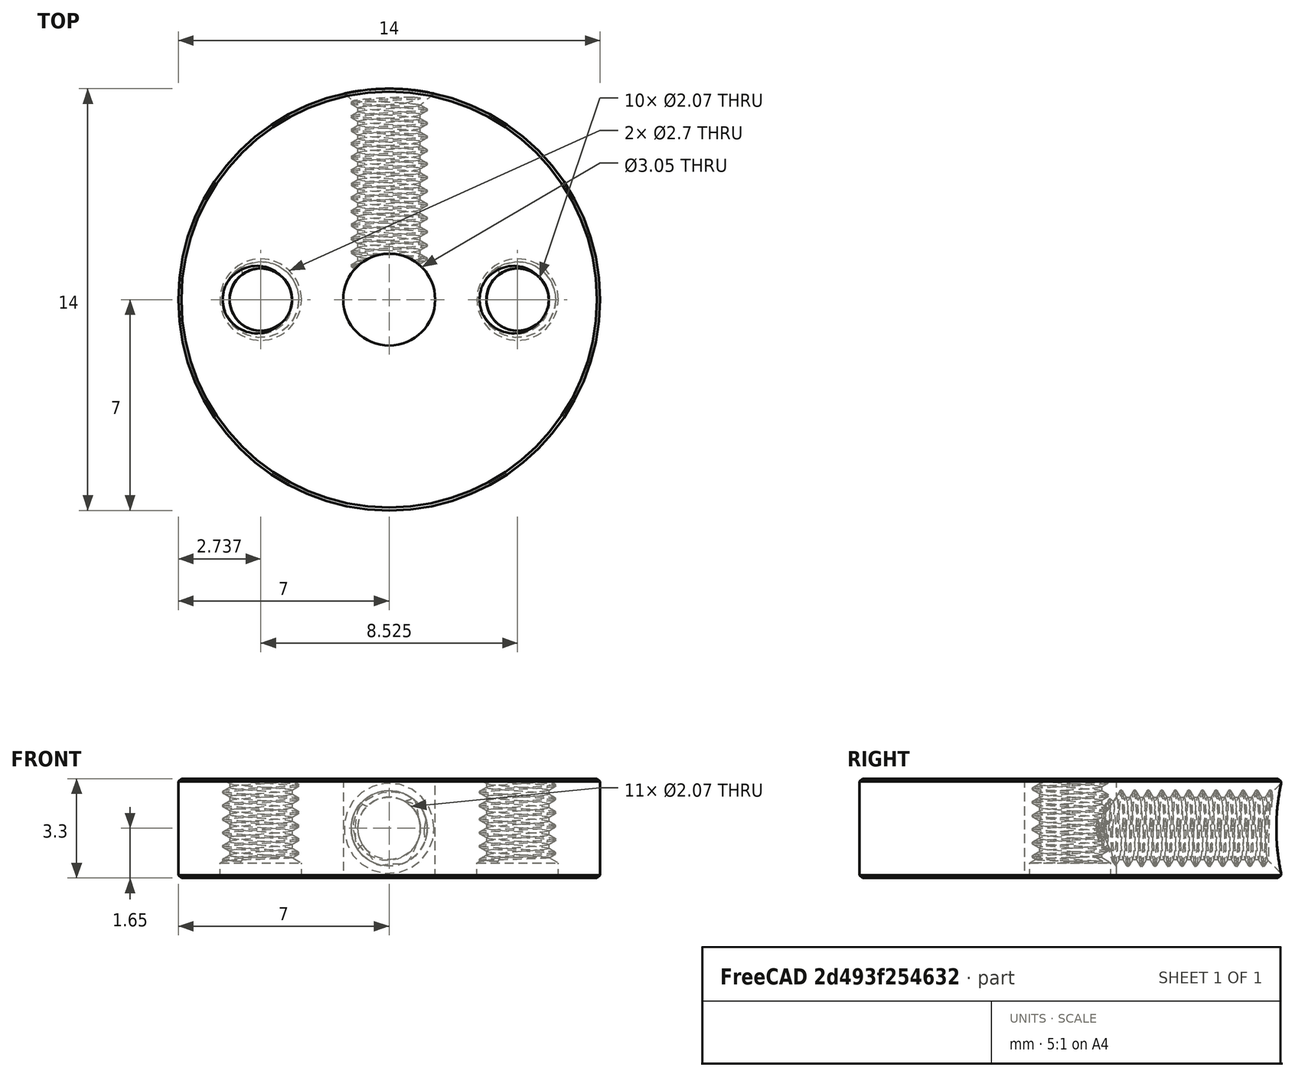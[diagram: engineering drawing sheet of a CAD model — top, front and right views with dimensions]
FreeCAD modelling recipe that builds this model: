
FCSTD DOCUMENT  (FreeCAD 0.20R29603 (Git))
Label: shaft-collar-relieved
License: Other
objects: TechDraw::DrawViewAnnotation×5, TechDraw::DrawViewDimension×4, Sketcher::SketchObject×3, PartDesign::Hole×3, TechDraw::DrawProjGroupItem×3, TechDraw::DrawViewSection×3, TechDraw::DrawViewBalloon×3, PartDesign::Chamfer×2, PartDesign::Pad×1, TechDraw::DrawSVGTemplate×1, PartDesign::Plane×1, PartDesign::Pocket×1, PartDesign::Body×1, TechDraw::DrawProjGroup×1, TechDraw::DrawRichAnno×1, TechDraw::DrawLeaderLine×1, TechDraw::DrawPage×1
note: 19 computed .brp shape members not serialized (recipe doc carries the construction recipe); baked Part::Feature solids carry a one-line shape summary decoded from their .brp

FEATURE [Sketcher::SketchObject] Sketch
  FullyConstrained = true
  MapMode = 5
  Support = -> [XY_Plane]
  sketch-geometry (5):
    g0: Circle CenterX=0 CenterY=0 CenterZ=0 NormalX=0 NormalY=0 NormalZ=1 AngleXU=0 Radius=7
    g1: Circle CenterX=0 CenterY=0 CenterZ=0 NormalX=0 NormalY=0 NormalZ=1 AngleXU=0 Radius=1.525
    g2: LineSegment StartX=1.525 StartY=0 StartZ=0 EndX=7 EndY=0 EndZ=0
    g3: Circle CenterX=4.2625 CenterY=0 CenterZ=0 NormalX=0 NormalY=0 NormalZ=1 AngleXU=0 Radius=1
    g4: Circle CenterX=-4.2625 CenterY=0 CenterZ=0 NormalX=0 NormalY=0 NormalZ=1 AngleXU=0 Radius=1
  constraints (15):
    c: Coincident(g1,g0)
    c: Coincident(g0,g-1)
    c: Diameter(g1) = 3.05
    c: Diameter(g0) = 14
    c: PointOnObject(g2,g1)
    c: PointOnObject(g2,g0)
    c: Horizontal(g2)
    c: PointOnObject(g2,g-1)
    c: DistanceX(g2,g2) = 5.475
    c: Symmetric(g2,g2,g3)
    c: Diameter(g3) = 2
    c: DistanceX(g2,g3) = 2.7375
    c: Symmetric(g3,g4,g-2)
    c: Equal(g4,g3)
    c: DistanceX(g4,g3) = 8.525
FEATURE [PartDesign::Pad] Pad
  Direction = (0,0,1)
  Length = 3.3
  Length2 = 10
  Profile = -> Sketch
  ReferenceAxis = -> Sketch [N_Axis]
  Type = 0
FEATURE [Sketcher::SketchObject] Sketch001
  ExternalGeometry = -> [Pad,Sketch]
  FullyConstrained = true
  MapMode = 5
  Placement = pos=(0,0,0) rot=(1,0,0;1.5708rad)
  Support = -> [XZ_Plane]
  sketch-geometry (3):
    g0: GeomPoint X=0 Y=1.65 Z=0
    g1: Circle CenterX=0 CenterY=1.65 CenterZ=0 NormalX=0 NormalY=0 NormalZ=1 AngleXU=0 Radius=1
    g2: LineSegment StartX=0 StartY=0 StartZ=0 EndX=0 EndY=3.3 EndZ=0
  constraints (7):
    c: PointOnObject(g0,g-2)
    c: Coincident(g1,g0)
    c: DistanceY(g-1,g1) = 1.65
    c: Coincident(g2,g-1)
    c: PointOnObject(g2,g-3)
    c: Symmetric(g2,g2,g1)
    c: Diameter(g1) = 2
FEATURE [TechDraw::DrawSVGTemplate] Template
  EditableTexts = Designed_by_Name=Lucian Chapar; Drawing_number=N/A; FC-Date=2023-02-15; FC-SC=4:1; FC-SH=1 OF 1; FC-Title=drive-wheel-shaft-collar-alt; Weight=N/A
  Height = 210
  Orientation = 1
  Width = 297
FEATURE [PartDesign::Hole] Hole
  BaseFeature = -> Pad
  CustomThreadClearance = 0
  Depth = 0.5
  DepthType = 0
  Diameter = 2.7
  DrillForDepth = false
  DrillPoint = 1
  DrillPointAngle = 118
  HoleCutCountersinkAngle = 90
  HoleCutCustomValues = false
  HoleCutDepth = 0
  HoleCutDiameter = 6.1
  HoleCutType = 0
  ModelThread = false
  Profile = -> Pad [Edge8,Edge11]
  Reversed = true
  Tapered = false
  TaperedAngle = 90
  ThreadClass = 0
  ThreadDepth = 0.5
  ThreadDepthType = 0
  ThreadDirection = 0
  ThreadFit = 0
  ThreadSize = 0
  ThreadType = 0
  Threaded = false
  UseCustomThreadClearance = false
FEATURE [PartDesign::Hole] Hole001
  BaseFeature = -> Hole
  CustomThreadClearance = 0
  Depth = 25
  DepthType = 0
  Diameter = 2.07
  DrillForDepth = false
  DrillPoint = 1
  DrillPointAngle = 118
  HoleCutCountersinkAngle = 90
  HoleCutCustomValues = false
  HoleCutDepth = 0
  HoleCutDiameter = 6.1
  HoleCutType = 0
  ModelThread = true
  Profile = -> Hole [Edge9,Edge8]
  Tapered = false
  TaperedAngle = 90
  ThreadClass = 0
  ThreadDepth = 25
  ThreadDepthType = 0
  ThreadDirection = 0
  ThreadFit = 0
  ThreadSize = 8
  ThreadType = 1
  Threaded = true
  UseCustomThreadClearance = false
FEATURE [PartDesign::Plane] DatumPlane
  AttachmentOffset = pos=(0,0,-7) rot=(0,0,1;0rad)
  Length = 60
  MapMode = 5
  Placement = pos=(0,7,1.6e-15) rot=(1,0,0;1.5708rad)
  ResizeMode = 0
  Support = -> [XZ_Plane]
  Width = 60
FEATURE [Sketcher::SketchObject] Sketch002
  ExternalGeometry = -> [Sketch001]
  FullyConstrained = true
  MapMode = 5
  Placement = pos=(0,7,1.6e-15) rot=(1,0,0;1.5708rad)
  Support = -> [DatumPlane]
  sketch-geometry (1):
    g0: Circle CenterX=0 CenterY=1.65 CenterZ=0 NormalX=0 NormalY=0 NormalZ=1 AngleXU=0 Radius=1
  constraints (3):
    c: Coincident(g0,g-3)
    c: Diameter(g-3) = 2
    c: Diameter(g0) = 2
FEATURE [PartDesign::Pocket] Pocket
  BaseFeature = -> Hole001
  Direction = (0,1,2e-16)
  Length = 7
  Length2 = 5
  Profile = -> Sketch002
  ReferenceAxis = -> Sketch002 [N_Axis]
  Reversed = true
  Type = 0
FEATURE [PartDesign::Chamfer] Chamfer
  Angle = 45
  Base = -> Pocket [Edge5,Edge4,Edge6]
  BaseFeature = -> Pocket
  ChamferType = 0
  FlipDirection = false
  Size = 0.5
  Size2 = 1
  SupportTransform = false
  UseAllEdges = false
FEATURE [PartDesign::Hole] Hole002
  BaseFeature = -> Chamfer
  CustomThreadClearance = 0
  Depth = 25
  DepthType = 0
  Diameter = 2.07
  DrillForDepth = false
  DrillPoint = 1
  DrillPointAngle = 118
  HoleCutCountersinkAngle = 90
  HoleCutCustomValues = false
  HoleCutDepth = 0
  HoleCutDiameter = 6.1
  HoleCutType = 0
  ModelThread = true
  Profile = -> Sketch001
  Tapered = false
  TaperedAngle = 90
  ThreadClass = 0
  ThreadDepth = 25
  ThreadDepthType = 0
  ThreadDirection = 0
  ThreadFit = 0
  ThreadSize = 8
  ThreadType = 1
  Threaded = true
  UseCustomThreadClearance = false
FEATURE [TechDraw::DrawViewAnnotation] Annotation
  Font = osifont
  LineSpace = 80
  LockPosition = false
  MaxWidth = -1
  Rotation = 0
  ScaleType = 0
  Text = Section A-A
  TextSize = 5
  TextStyle = 0
  X = 213.839
  Y = 106.01
FEATURE [TechDraw::DrawViewAnnotation] Annotation001
  Font = osifont
  LineSpace = 80
  LockPosition = false
  MaxWidth = -1
  Rotation = 0
  ScaleType = 0
  Text = Section B-B
  TextSize = 5
  TextStyle = 0
  X = 213.919
  Y = 187.915
FEATURE [TechDraw::DrawViewAnnotation] Annotation002
  Font = osifont
  LineSpace = 80
  LockPosition = false
  MaxWidth = -1
  Rotation = 0
  ScaleType = 0
  Text = Section C - C
  TextSize = 5
  TextStyle = 0
  X = 265.047
  Y = 115.508
FEATURE [TechDraw::DrawViewAnnotation] Annotation003
  Font = osifont
  LineSpace = 80
  LockPosition = false
  MaxWidth = -1
  Rotation = 0
  ScaleType = 0
  Text = OPULO INC
  TextSize = 5
  TextStyle = 0
  X = 203.475
  Y = 31.1769
FEATURE [PartDesign::Chamfer] Chamfer001
  Angle = 45
  Base = -> Hole002 [Edge2,Edge4]
  BaseFeature = -> Hole002
  ChamferType = 0
  FlipDirection = false
  Size = 0.1
  Size2 = 1
  SupportTransform = false
  UseAllEdges = false
FEATURE [PartDesign::Body] Body
  Group = -> [Sketch,Pad,Sketch001,Hole,Hole001,DatumPlane,Sketch002,Pocket,Chamfer,Hole002,Chamfer001]
  Origin = -> Origin
  Tip = -> Chamfer001
FEATURE [TechDraw::DrawProjGroupItem] ProjItem  label="Top002"
  CoarseView = false
  Direction = (0,0,1)
  Focus = 100
  HardHidden = false
  IsoCount = 0
  IsoHidden = false
  IsoVisible = false
  LockPosition = true
  Perspective = false
  Rotation = 0
  RotationVector = (1,0,0)
  Scale = 4
  ScaleType = 2
  SeamHidden = false
  SeamVisible = true
  SmoothHidden = false
  SmoothVisible = true
  Source = -> [Body]
  Type = 5
  X = 0
  XDirection = (1,0,0)
  Y = 0
FEATURE [TechDraw::DrawProjGroupItem] ProjItem001  label="Front"
  CoarseView = false
  Direction = (0,1,0)
  Focus = 100
  HardHidden = false
  IsoCount = 0
  IsoHidden = false
  IsoVisible = false
  LockPosition = false
  Perspective = false
  Rotation = 0
  RotationVector = (1,0,0)
  ScaleType = 2
  SeamHidden = false
  SeamVisible = true
  SmoothHidden = false
  SmoothVisible = true
  Source = -> [Body]
  Type = 4
  X = 0
  XDirection = (1,0,0)
  Y = -55.9883
FEATURE [TechDraw::DrawProjGroupItem] ProjItem002  label="Left"
  CoarseView = false
  Direction = (-1,0,1e-16)
  Focus = 100
  HardHidden = false
  IsoCount = 0
  IsoHidden = false
  IsoVisible = false
  LockPosition = false
  Perspective = false
  Rotation = 0
  RotationVector = (1,0,0)
  ScaleType = 2
  SeamHidden = false
  SeamVisible = true
  SmoothHidden = false
  SmoothVisible = true
  Source = -> [Body]
  Type = 1
  X = 55
  XDirection = (1e-16,0,1)
  Y = 0
FEATURE [TechDraw::DrawProjGroup] ProjGroup
  Anchor = -> ProjItem
  AutoDistribute = false
  LockPosition = false
  ProjectionType = 0
  Rotation = 0
  Scale = 4
  ScaleType = 2
  Source = -> [Body]
  Views = -> [ProjItem,ProjItem001,ProjItem002]
  X = 61.8769
  Y = 150
  spacingX = 15
  spacingY = 15
FEATURE [TechDraw::DrawViewSection] SectionView001  label="Section A - A"
  BaseView = -> ProjItem
  CoarseView = false
  CutSurfaceDisplay = 2
  Direction = (0,-1,0)
  FileGeomPattern = /Applications/FreeCAD.app/Contents/Resources/share/Mod/TechDraw/PAT/FCPAT.pat
  FileHatchPattern = /Applications/FreeCAD.app/Contents/Resources/share/Mod/TechDraw/Patterns/simple.svg
  Focus = 100
  FuseBeforeCut = false
  HardHidden = false
  HatchScale = 1
  IsoCount = 0
  IsoHidden = false
  IsoVisible = false
  LockPosition = false
  NameGeomPattern = Diamond
  Perspective = false
  Rotation = 0
  Scale = 4
  ScaleType = 2
  SeamHidden = false
  SeamVisible = true
  SectionDirection = 2
  SectionNormal = (0,-1,0)
  SectionOrigin = (0.013,0.003,1.65)
  SectionSymbol = A
  SmoothHidden = false
  SmoothVisible = true
  Source = -> [Body]
  X = 215.276
  XDirection = (1,0,0)
  Y = 93.815
FEATURE [TechDraw::DrawViewDimension] Dimension005
  AngleOverride = false
  Arbitrary = false
  ArbitraryTolerances = false
  EqualTolerance = false
  ExtensionAngle = 0
  FormatSpec = ⌀%.2w
  FormatSpecOverTolerance = %+.2w
  FormatSpecUnderTolerance = %+.2w
  Inverted = false
  LineAngle = 0
  LockPosition = false
  MeasureType = 1
  OverTolerance = 0
  References2D = -> [SectionView001]
  Rotation = 0
  ScaleType = 0
  TheoreticalExact = false
  Type = 1
  UnderTolerance = -0.2
  X = 35.0716
  Y = 16.5241
FEATURE [TechDraw::DrawViewBalloon] Balloon005
  BubbleShape = 1
  EndType = 0
  EndTypeScale = 1
  KinkLength = 5
  LockPosition = false
  OriginX = 0.164571
  OriginY = -1.02183
  Rotation = 0
  ScaleType = 0
  ShapeScale = 1
  SourceView = -> SectionView001
  Text = M2.5x0.45 ↧ 7
  TextWrapLen = -1
  X = 6.70793
  Y = -4.88619
FEATURE [TechDraw::DrawViewBalloon] Balloon006
  BubbleShape = 1
  EndType = 0
  EndTypeScale = 1
  KinkLength = 13
  LockPosition = false
  OriginX = -5.6125
  OriginY = -1.65
  Rotation = 0
  ScaleType = 0
  ShapeScale = 1
  SourceView = -> SectionView001
  TextWrapLen = -1
  X = -11.2435
  Y = -6.5218
FEATURE [TechDraw::DrawViewSection] SectionView  label="Section C - C"
  BaseView = -> ProjItem001
  CoarseView = false
  CutSurfaceDisplay = 2
  Direction = (-1,0,0)
  FileGeomPattern = /Applications/FreeCAD.app/Contents/Resources/share/Mod/TechDraw/PAT/FCPAT.pat
  FileHatchPattern = /Applications/FreeCAD.app/Contents/Resources/share/Mod/TechDraw/Patterns/simple.svg
  Focus = 100
  FuseBeforeCut = false
  HardHidden = false
  HatchScale = 1
  IsoCount = 0
  IsoHidden = false
  IsoVisible = false
  LockPosition = false
  NameGeomPattern = Diamond
  Perspective = false
  Rotation = 90
  Scale = 4
  ScaleType = 2
  SeamHidden = false
  SeamVisible = true
  SectionDirection = 0
  SectionNormal = (-1,0,0)
  SectionOrigin = (0.013,0.003,1.65)
  SectionSymbol = C
  SmoothHidden = false
  SmoothVisible = true
  Source = -> [Body]
  X = 265.52
  XDirection = (0,1,0)
  Y = 150
FEATURE [TechDraw::DrawViewSection] SectionView002  label="Section B - B"
  BaseView = -> ProjItem002
  CoarseView = false
  CutSurfaceDisplay = 2
  Direction = (1e-16,0,1)
  FileGeomPattern = /Applications/FreeCAD.app/Contents/Resources/share/Mod/TechDraw/PAT/FCPAT.pat
  FileHatchPattern = /Applications/FreeCAD.app/Contents/Resources/share/Mod/TechDraw/Patterns/simple.svg
  Focus = 100
  FuseBeforeCut = false
  HardHidden = false
  HatchScale = 1
  IsoCount = 0
  IsoHidden = false
  IsoVisible = false
  LockPosition = false
  NameGeomPattern = Diamond
  Perspective = false
  Rotation = 0
  Scale = 4
  ScaleType = 2
  SeamHidden = false
  SeamVisible = true
  SectionDirection = 1
  SectionNormal = (1e-16,0,1)
  SectionOrigin = (0.013,0.003,1.65)
  SectionSymbol = B
  SmoothHidden = false
  SmoothVisible = true
  Source = -> [Body]
  X = 213.104
  XDirection = (1,0,-1e-16)
  Y = 150
FEATURE [TechDraw::DrawRichAnno] RichTextAnnotation002
  AnnoParent = -> Balloon006
  AnnoText = <!DOCTYPE HTML PUBLIC "-//W3C//DTD HTML 4.0//EN" "http://www.w3.org/TR/REC-html40/strict.dtd">\n<html><head><meta name="qrichtext" content="1" /><style type="text/css">\np, li { white-space: pre-wrap; }\n</style></head><body style=" font-family:'.AppleSystemUIFont'; font-size:13pt; font-weight:400; font-style:normal;">\n<p style=" margin-top:0px; margin-bottom:0px; margin-left:0px; margin-right:0px; -qt-block-indent:0; text-indent:0px;">2x ⌴ <span style=" font-size:15pt;">⌀</span>0.27 ↧ x 0.5</p>\n<p style=" margin-top:0px; margin-bottom:0px; margin-left:0px; margin-right:0px; -qt-block-indent:0; text-indent:0px;">M2.5x0.45 THRU ALL</p></body></html>
  LockPosition = false
  MaxWidth = -1
  Rotation = 0
  ScaleType = 0
  ShowFrame = false
  X = -63.1014
  Y = -28.2154
FEATURE [TechDraw::DrawViewDimension] Dimension
  AngleOverride = false
  Arbitrary = false
  ArbitraryTolerances = false
  EqualTolerance = true
  ExtensionAngle = 0
  FormatSpec = %.3w
  FormatSpecOverTolerance = %+.3w
  FormatSpecUnderTolerance = %+.3w
  Inverted = false
  LineAngle = 0
  LockPosition = false
  MeasureType = 1
  OverTolerance = 0.03
  References2D = -> [SectionView002]
  Rotation = 0
  ScaleType = 0
  TheoreticalExact = false
  Type = 1
  UnderTolerance = -0.03
  X = -35.3715
  Y = 37.0784
FEATURE [TechDraw::DrawViewDimension] Dimension006
  AngleOverride = false
  Arbitrary = false
  ArbitraryTolerances = false
  EqualTolerance = false
  ExtensionAngle = 0
  FormatSpec = ⌀%.2w
  FormatSpecOverTolerance = %+.2w
  FormatSpecUnderTolerance = %+.2w
  Inverted = false
  LineAngle = 0
  LockPosition = false
  MeasureType = 1
  OverTolerance = 0
  References2D = -> [SectionView002]
  Rotation = 0
  ScaleType = 0
  TheoreticalExact = false
  Type = 5
  UnderTolerance = -0.02
  X = -50.3873
  Y = -13.4628
FEATURE [TechDraw::DrawViewBalloon] Balloon
  BubbleShape = 1
  EndType = 0
  EndTypeScale = 1
  KinkLength = 5
  LockPosition = false
  OriginX = -1.2784
  OriginY = 6.77847
  Rotation = 0
  ScaleType = 0
  ShapeScale = 1
  SourceView = -> SectionView
  Text = 0.5x45°
  TextWrapLen = -1
  X = 3.02066
  Y = 9.11529
FEATURE [TechDraw::DrawViewDimension] Dimension007
  AngleOverride = false
  Arbitrary = false
  ArbitraryTolerances = false
  EqualTolerance = false
  ExtensionAngle = 0
  FormatSpec = %.2w
  FormatSpecOverTolerance = %+.2w
  FormatSpecUnderTolerance = %+.2w
  Inverted = false
  LineAngle = 0
  LockPosition = false
  MeasureType = 1
  OverTolerance = 0
  References2D = -> [SectionView001]
  Rotation = 0
  ScaleType = 0
  TheoreticalExact = false
  Type = 2
  UnderTolerance = -0.1
  X = -47.1492
  Y = 18.955
FEATURE [TechDraw::DrawLeaderLine] LeaderLine
  AutoHorizontal = true
  EndSymbol = 0
  LeaderParent = -> SectionView001
  LockPosition = true
  Rotation = 0
  Scalable = false
  ScaleType = 0
  StartSymbol = 0
  WayPoints = (3) [(0,0,0),(188.878,118.061,0),(1.56712,118.061,0)]
  X = 6.95016
  Y = 1.5497
FEATURE [TechDraw::DrawViewAnnotation] Annotation004
  Font = osifont
  LineSpace = 80
  LockPosition = false
  MaxWidth = -1
  Rotation = 0
  ScaleType = 0
  Text = 0.1x45°
  TextSize = 5
  TextStyle = 0
  X = 270.427
  Y = 85.6893
FEATURE [TechDraw::DrawPage] Page
  KeepUpdated = true
  NextBalloonIndex = 9
  ProjectionType = 0
  Template = -> Template
  Views = -> [ProjGroup,SectionView001,Dimension005,Balloon005,Balloon006,SectionView,SectionView002,RichTextAnnotation002,Dimension,Dimension006,Balloon,Annotation,Annotation001,Annotation002,Annotation003,Dimension007,LeaderLine,Annotation004]
